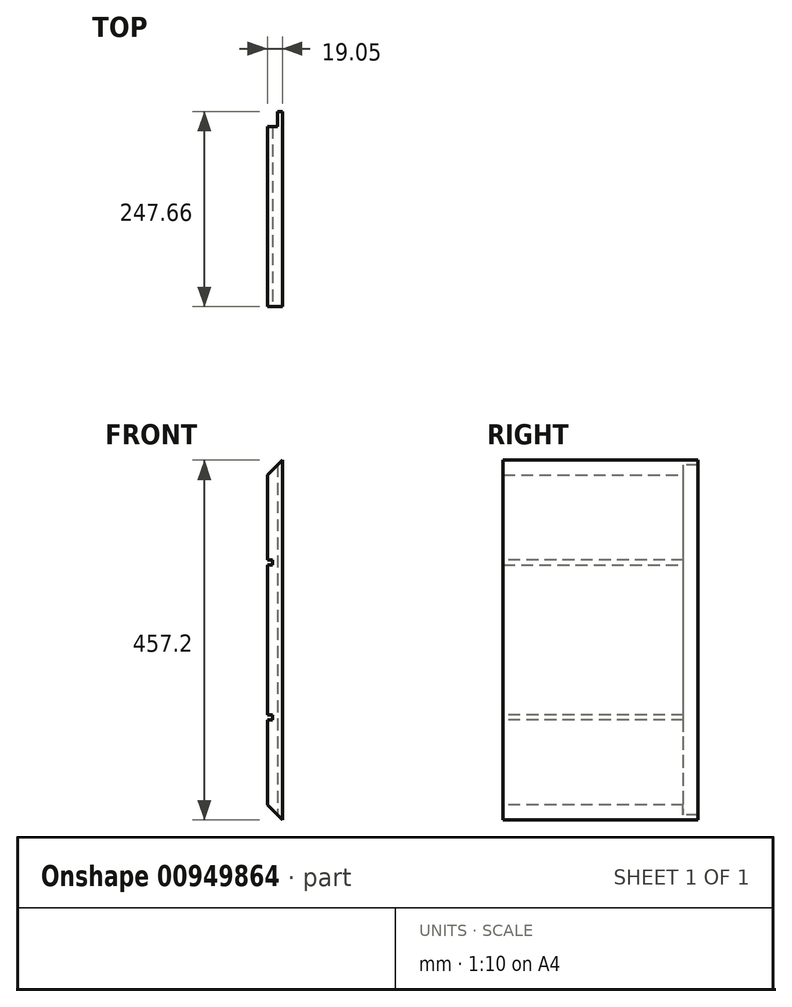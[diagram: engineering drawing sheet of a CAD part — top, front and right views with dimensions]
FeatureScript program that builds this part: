
annotation { "Feature Type Name" : "Feature", "Feature Type Description" : "" }
export const myFeature = defineFeature(function(context is Context, id is Id, definition is map)
    precondition{}
    {
        {
            var Q0;
            Q0=qCreatedBy(makeId("Right.planeOp"),FACE);
            var sketch = newSketch(context, id + "F0", { "sketchPlane" : qUnion([Q0])});
            skLineSegment(sketch, "E0.bottom", {"start": v(123.83, -228.6) * mm, "end": v(-123.83, -228.6) * mm});
            skLineSegment(sketch, "E0.top", {"start": v(123.83, 228.6) * mm, "end": v(-123.82, 228.6) * mm});
            skLineSegment(sketch, "E0.left", {"start": v(123.83, -228.6) * mm, "end": v(123.83, 228.6) * mm});
            skLineSegment(sketch, "E0.right", {"start": v(-123.83, -228.6) * mm, "end": v(-123.83, 228.6) * mm});
            skPoint(sketch, "E0.middle", {"position": v(0, 0) * mm});
            skSolve(sketch);
        }
        {
            var Q0;
            Q0 = qSketchRegion(id + "F0", true);
            extrude(context, id + "F1", {"entities" : qUnion([Q0]), "depth" : 19.05 * mm, "offsetDistance" : 25.4 * mm});
        }
        {
            var Q0;
            Q0=makeQuery(id+"F1.opExtrude","SWEPT_FACE",FACE,{"disambiguationData":[OSD([sQuery(id+"F0.wireOp",EDGE,"E0.bottom")])]});
            var sketch = newSketch(context, id + "F2", { "sketchPlane" : qUnion([Q0])});
            skLineSegment(sketch, "E1", {"start": v(12.7, -123.82) * mm, "end": v(12.7, -104.77) * mm});
            skLineSegment(sketch, "E2", {"start": v(12.7, -104.77) * mm, "end": v(0, -104.77) * mm});
            skLineSegment(sketch, "E3", {"start": v(0, -104.77) * mm, "end": v(0, -123.82) * mm});
            skLineSegment(sketch, "E4", {"start": v(0, -123.82) * mm, "end": v(12.7, -123.82) * mm});
            skSolve(sketch);
        }
        {
            var Q0;
            Q0 = qSketchRegion(id + "F2", true);
            extrude(context, id + "F3", {"entities" : qUnion([Q0]), "operationType" : NewBodyOperationType.REMOVE, "endBound" : BoundingType.THROUGH_ALL, "oppositeDirection" : true, "depth" : 25.4 * mm, "offsetDistance" : 25.4 * mm});
        }
        {
            var Q0;
            Q0=makeQuery(id+"F1.opExtrude","CAP_EDGE",EDGE,{"disambiguationData":[OSD([sQuery(id+"F0.wireOp",EDGE,"E0.top")])],"isStart":true});
            chamfer(context, id + "F4", {"entities" : qUnion([Q0]), "width" : 19.05 * mm, "tangentPropagation" : true});
        }
        {
            var Q0;
            Q0=makeQuery(id+"F1.opExtrude","CAP_EDGE",EDGE,{"disambiguationData":[OSD([sQuery(id+"F0.wireOp",EDGE,"E0.bottom")])],"isStart":true});
            chamfer(context, id + "F5", {"entities" : qUnion([Q0]), "width" : 19.05 * mm, "tangentPropagation" : true});
        }
        {
            var Q0;
            Q0=makeQuery(id+"F1.opExtrude","CAP_FACE",FACE,{"disambiguationData":[OSD([sQuery(id+"F0.wireOp",EDGE,"E0.bottom"),sQuery(id+"F0.wireOp",EDGE,"E0.top"),sQuery(id+"F0.wireOp",EDGE,"E0.left"),sQuery(id+"F0.wireOp",EDGE,"E0.right")])],"isStart":true});
            var sketch = newSketch(context, id + "F6", { "sketchPlane" : qUnion([Q0])});
            skLineSegment(sketch, "E5", {"start": v(-104.77, -95.25) * mm, "end": v(123.83, -95.25) * mm});
            skLineSegment(sketch, "E6", {"start": v(-104.77, -101.6) * mm, "end": v(123.83, -101.6) * mm});
            skLineSegment(sketch, "E7", {"start": v(123.83, -95.25) * mm, "end": v(123.83, -101.6) * mm});
            skLineSegment(sketch, "E8", {"start": v(-104.77, -95.25) * mm, "end": v(-104.77, -101.6) * mm});
            skLineSegment(sketch, "E9", {"start": v(-104.77, 101.6) * mm, "end": v(123.83, 101.6) * mm});
            skLineSegment(sketch, "E10", {"start": v(123.83, 101.6) * mm, "end": v(123.83, 95.25) * mm});
            skLineSegment(sketch, "E11", {"start": v(123.83, 95.25) * mm, "end": v(-104.77, 95.25) * mm});
            skLineSegment(sketch, "E12", {"start": v(-104.78, 95.25) * mm, "end": v(-104.78, 101.6) * mm});
            skSolve(sketch);
        }
        {
            var Q0;
            Q0 = qSketchRegion(id + "F6", true);
            extrude(context, id + "F7", {"entities" : qUnion([Q0]), "operationType" : NewBodyOperationType.REMOVE, "oppositeDirection" : true, "depth" : 6.35 * mm, "offsetDistance" : 25.4 * mm});
        }
    });
